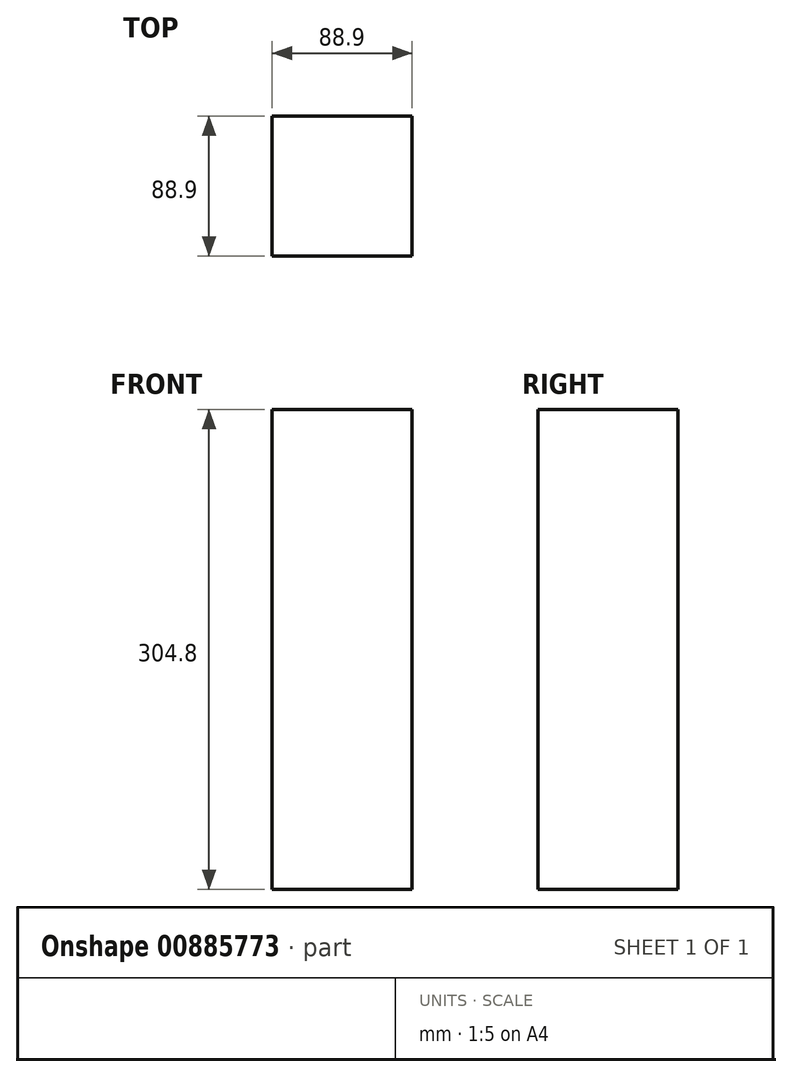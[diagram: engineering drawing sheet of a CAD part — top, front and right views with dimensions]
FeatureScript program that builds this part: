
annotation { "Feature Type Name" : "Feature", "Feature Type Description" : "" }
export const myFeature = defineFeature(function(context is Context, id is Id, definition is map)
    precondition{}
    {
        {
            var Q0;
            Q0=qCreatedBy(makeId("Top.planeOp"),FACE);
            var sketch = newSketch(context, id + "F0", { "sketchPlane" : qUnion([Q0])});
            skLineSegment(sketch, "E0.bottom", {"start": v(44.45, -44.45) * mm, "end": v(-44.45, -44.45) * mm});
            skLineSegment(sketch, "E0.top", {"start": v(44.45, 44.45) * mm, "end": v(-44.45, 44.45) * mm});
            skLineSegment(sketch, "E0.left", {"start": v(44.45, -44.45) * mm, "end": v(44.45, 44.45) * mm});
            skLineSegment(sketch, "E0.right", {"start": v(-44.45, -44.45) * mm, "end": v(-44.45, 44.45) * mm});
            skPoint(sketch, "E0.middle", {"position": v(0, 0) * mm});
            skSolve(sketch);
        }
        {
            var Q0;
            Q0=makeQuery(id+"F0.imprint","IMPRINT",FACE,{"disambiguationData":[TD([[makeQuery(id+"F0.imprint","IMPRINT",EDGE,{"derivedFrom":sQuery(id+"F0.wireOp",EDGE,"E0.bottom")}),-1.0]])]});
            extrude(context, id + "F1", {"entities" : qUnion([Q0]), "endBound" : BoundingType.SYMMETRIC, "depth" : 304.8 * mm, "offsetDistance" : 25.4 * mm});
        }
    });
